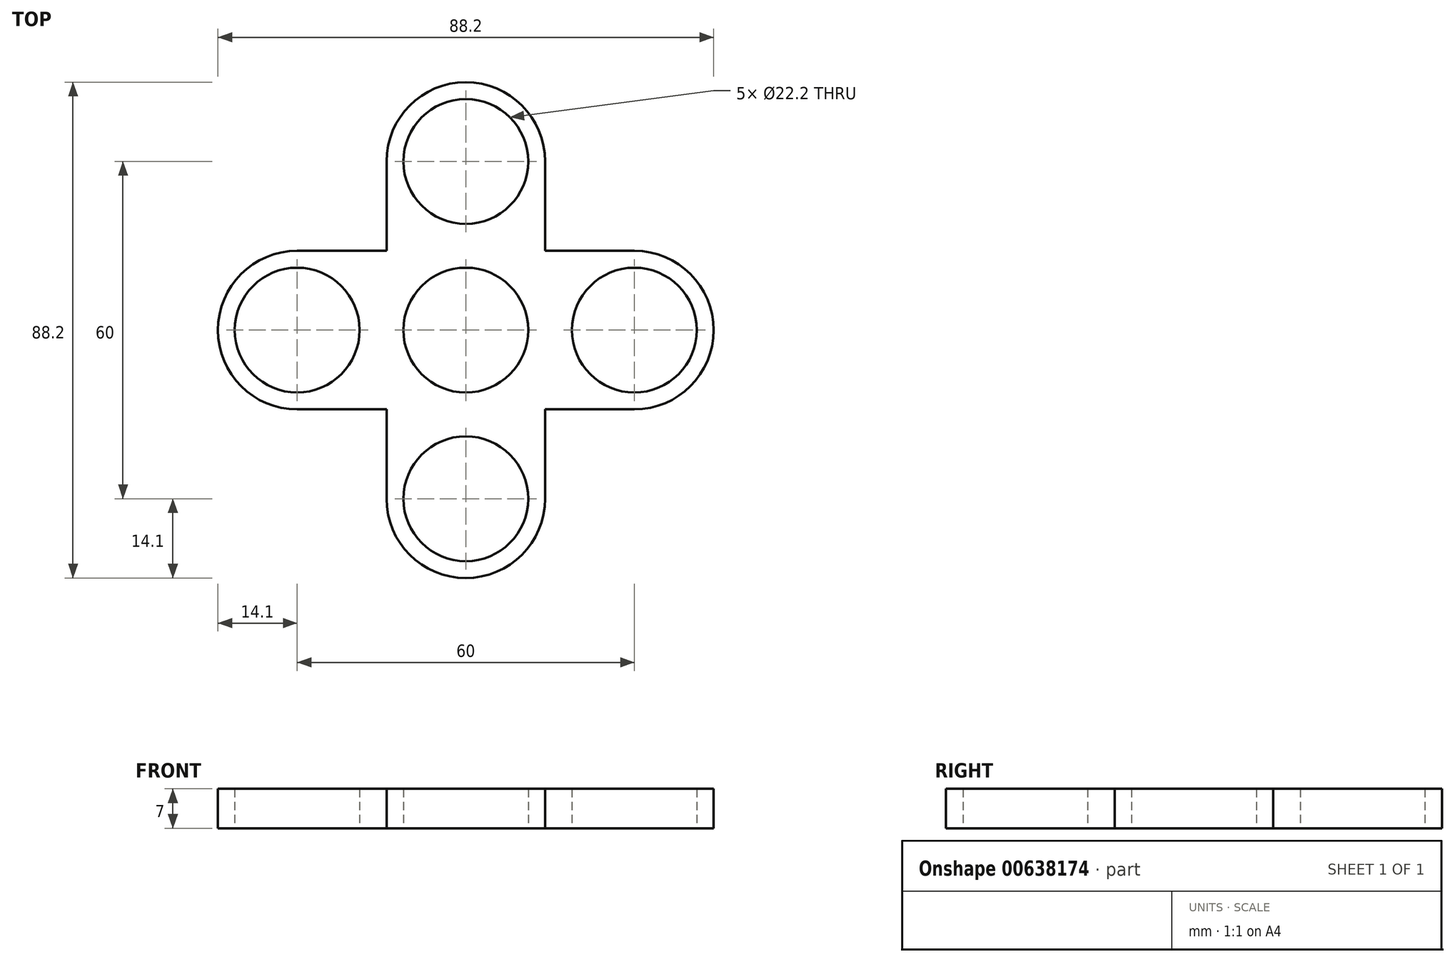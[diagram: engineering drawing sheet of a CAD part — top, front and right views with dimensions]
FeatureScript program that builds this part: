
annotation { "Feature Type Name" : "Feature", "Feature Type Description" : "" }
export const myFeature = defineFeature(function(context is Context, id is Id, definition is map)
    precondition{}
    {
        {
            var Q0;
            Q0=qCreatedBy(makeId("Top.planeOp"),FACE);
            var sketch = newSketch(context, id + "F0", { "sketchPlane" : qUnion([Q0])});
            skCircle(sketch, "E0", {"center": v(0, 0) * mm, "radius": 11.1 * mm});
            skCircle(sketch, "E1", {"center": v(0, 30) * mm, "radius": 11.1 * mm});
            skCircle(sketch, "E2.1.0", {"center": v(-30, 0) * mm, "radius": 11.1 * mm});
            skCircle(sketch, "E2.2.0", {"center": v(0, -30) * mm, "radius": 11.1 * mm});
            skCircle(sketch, "E2.3.0", {"center": v(30, 0) * mm, "radius": 11.1 * mm});
            skArc(sketch, "E3.0", {"start": v(14.1, 30) * mm, "mid": v(0, 44.1) * mm, "end": v(-14.1, 30) * mm});
            skLineSegment(sketch, "E4", {"start": v(14.1, 30) * mm, "end": v(14.1, 14.1) * mm});
            skLineSegment(sketch, "E5", {"start": v(-14.1, 30) * mm, "end": v(-14.1, 14.1) * mm});
            skLineSegment(sketch, "E6.1.0", {"start": v(-30, 14.1) * mm, "end": v(-14.1, 14.1) * mm});
            skLineSegment(sketch, "E6.1.1", {"start": v(-30, -14.1) * mm, "end": v(-14.1, -14.1) * mm});
            skArc(sketch, "E6.1.2", {"start": v(-30, 14.1) * mm, "mid": v(-44.1, 0) * mm, "end": v(-30, -14.1) * mm});
            skLineSegment(sketch, "E6.2.0", {"start": v(-14.1, -30) * mm, "end": v(-14.1, -14.1) * mm});
            skLineSegment(sketch, "E6.2.1", {"start": v(14.1, -30) * mm, "end": v(14.1, -14.1) * mm});
            skArc(sketch, "E6.2.2", {"start": v(-14.1, -30) * mm, "mid": v(0, -44.1) * mm, "end": v(14.1, -30) * mm});
            skLineSegment(sketch, "E6.3.0", {"start": v(30, -14.1) * mm, "end": v(14.1, -14.1) * mm});
            skLineSegment(sketch, "E6.3.1", {"start": v(30, 14.1) * mm, "end": v(14.1, 14.1) * mm});
            skArc(sketch, "E6.3.2", {"start": v(30, -14.1) * mm, "mid": v(44.1, 0) * mm, "end": v(30, 14.1) * mm});
            skPoint(sketch, "E7.orphan", {"position": v(14.1, 3.54) * mm});
            skPoint(sketch, "E8.orphan", {"position": v(-14.1, -2.74) * mm});
            skPoint(sketch, "E9.orphan", {"position": v(-3.54, 14.1) * mm});
            skPoint(sketch, "E10.orphan", {"position": v(-2.74, 14.1) * mm});
            skPoint(sketch, "E11.orphan", {"position": v(-14.1, -3.54) * mm});
            skPoint(sketch, "E12.orphan", {"position": v(14.1, 2.74) * mm});
            skPoint(sketch, "E13.orphan", {"position": v(3.54, -14.1) * mm});
            skPoint(sketch, "E14.orphan", {"position": v(2.74, -14.1) * mm});
            skPoint(sketch, "E15.start.orphan", {"position": v(-15.25, 30) * mm});
            skSolve(sketch);
        }
        {
            var Q0;
            Q0=makeQuery(id+"F0.imprint","IMPRINT",FACE,{"disambiguationData":[TD([[makeQuery(id+"F0.imprint","IMPRINT",EDGE,{"derivedFrom":sQuery(id+"F0.wireOp",EDGE,"E0")}),-1.0]])]});
            extrude(context, id + "F1", {"entities" : qUnion([Q0]), "depth" : 7 * mm, "offsetDistance" : 25 * mm});
        }
    });
